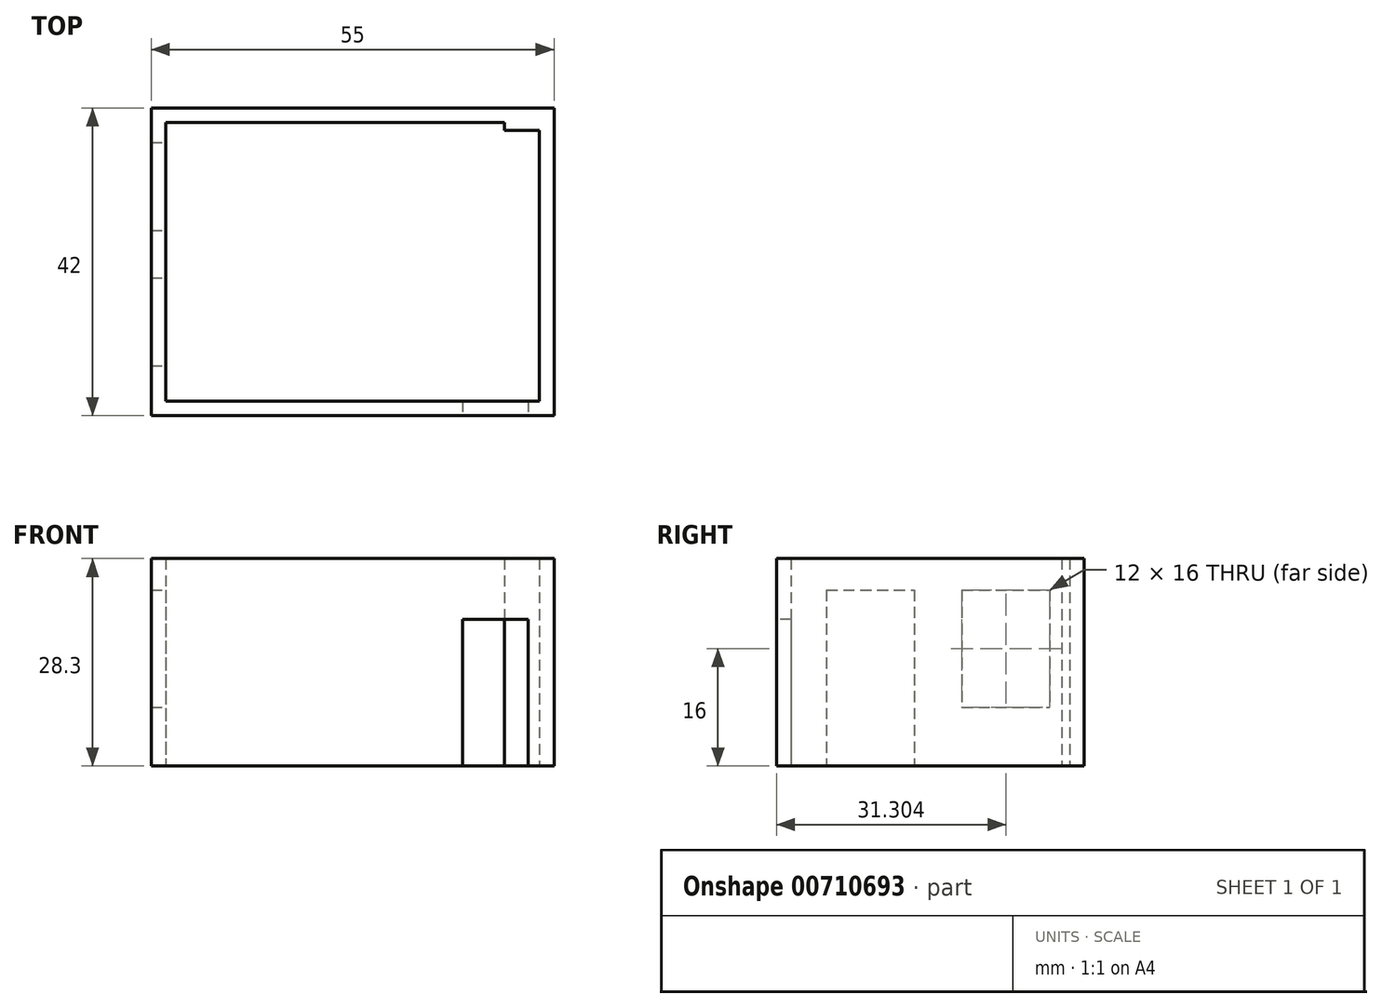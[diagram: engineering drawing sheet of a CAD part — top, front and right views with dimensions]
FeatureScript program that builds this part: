
annotation { "Feature Type Name" : "Feature", "Feature Type Description" : "" }
export const myFeature = defineFeature(function(context is Context, id is Id, definition is map)
    precondition{}
    {
        {
            var Q0;
            Q0=qCreatedBy(makeId("Top.planeOp"),FACE);
            var sketch = newSketch(context, id + "F0", { "sketchPlane" : qUnion([Q0])});
            skLineSegment(sketch, "E0.bottom", {"start": v(0.05, 41.89) * mm, "end": v(55.05, 41.89) * mm});
            skLineSegment(sketch, "E0.top", {"start": v(0.05, -0.11) * mm, "end": v(42.53, -0.11) * mm});
            skLineSegment(sketch, "E0.left", {"start": v(0.05, 41.89) * mm, "end": v(0.05, 37.2) * mm});
            skLineSegment(sketch, "E0.right", {"start": v(55.05, 41.89) * mm, "end": v(55.05, -0.11) * mm});
            skLineSegment(sketch, "E1.0", {"start": v(2.05, 39.89) * mm, "end": v(48.26, 39.89) * mm});
            skLineSegment(sketch, "E1.1", {"start": v(2.05, 39.89) * mm, "end": v(2.05, 37.2) * mm});
            skLineSegment(sketch, "E1.2", {"start": v(2.05, 1.89) * mm, "end": v(42.53, 1.89) * mm});
            skLineSegment(sketch, "E1.3", {"start": v(53.05, 38.83) * mm, "end": v(53.05, 1.89) * mm});
            skLineSegment(sketch, "E2", {"start": v(51.53, 1.89) * mm, "end": v(51.53, -0.11) * mm});
            skLineSegment(sketch, "E3", {"start": v(42.53, 1.89) * mm, "end": v(42.53, -0.11) * mm});
            skLineSegment(sketch, "E4", {"start": v(0.05, 37.2) * mm, "end": v(2.05, 37.2) * mm});
            skLineSegment(sketch, "E5", {"start": v(0.05, 25.2) * mm, "end": v(2.05, 25.2) * mm});
            skLineSegment(sketch, "E6", {"start": v(0.05, 18.72) * mm, "end": v(2.05, 18.72) * mm});
            skLineSegment(sketch, "E7", {"start": v(0.05, 6.72) * mm, "end": v(2.05, 6.72) * mm});
            skLineSegment(sketch, "E8.top", {"start": v(48.26, 38.83) * mm, "end": v(53.05, 38.83) * mm});
            skLineSegment(sketch, "E8.left", {"start": v(48.26, 39.89) * mm, "end": v(48.26, 38.83) * mm});
            skLineSegment(sketch, "E9.trimOffspring", {"start": v(51.53, -0.11) * mm, "end": v(55.05, -0.11) * mm});
            skLineSegment(sketch, "E10.trimOffspring", {"start": v(51.53, 1.89) * mm, "end": v(53.05, 1.89) * mm});
            skLineSegment(sketch, "E11.trimOffspring", {"start": v(2.05, 25.2) * mm, "end": v(2.05, 18.72) * mm});
            skLineSegment(sketch, "E12.trimOffspring", {"start": v(0.05, 25.2) * mm, "end": v(0.05, 18.72) * mm});
            skLineSegment(sketch, "E13.trimOffspring", {"start": v(0.05, 6.72) * mm, "end": v(0.05, -0.11) * mm});
            skLineSegment(sketch, "E14.trimOffspring", {"start": v(2.05, 6.72) * mm, "end": v(2.05, 1.89) * mm});
            skSolve(sketch);
        }
        {
            var Q0;
            Q0 = qSketchRegion(id + "F0", true);
            extrude(context, id + "F1", {"entities" : qUnion([Q0]), "depth" : 28.3 * mm, "offsetDistance" : 25 * mm});
        }
        {
            var Q0;
            Q0=makeQuery(id+"F1.opExtrude","SWEPT_FACE",FACE,{"disambiguationData":[OSD([sQuery(id+"F0.wireOp",EDGE,"E4")])]});
            var sketch = newSketch(context, id + "F2", { "sketchPlane" : qUnion([Q0])});
            skLineSegment(sketch, "E15.bottom", {"start": v(0.05, 8) * mm, "end": v(2.05, 8) * mm});
            skLineSegment(sketch, "E15.top", {"start": v(0.05, 0) * mm, "end": v(2.05, 0) * mm});
            skLineSegment(sketch, "E15.left", {"start": v(0.05, 8) * mm, "end": v(0.05, 0) * mm});
            skLineSegment(sketch, "E15.right", {"start": v(2.05, 8) * mm, "end": v(2.05, 0) * mm});
            skLineSegment(sketch, "E16.0", {"start": v(2.05, 28.3) * mm, "end": v(2.05, 0) * mm});
            skLineSegment(sketch, "E17.0", {"start": v(0.05, 28.3) * mm, "end": v(0.05, 0) * mm});
            skSolve(sketch);
        }
        {
            var Q0;
            Q0=makeQuery(id+"F2.imprint","IMPRINT",FACE,{"disambiguationData":[TD([[makeQuery(id+"F2.imprint","IMPRINT",EDGE,{"derivedFrom":sQuery(id+"F2.wireOp",EDGE,"E15.bottom")}),-1.0]])]});
            extrude(context, id + "F3", {"entities" : qUnion([Q0]), "operationType" : NewBodyOperationType.ADD, "depth" : 12 * mm, "offsetDistance" : 25 * mm});
        }
        {
            var Q0;
            Q0=makeQuery(id+"F1.opExtrude","SWEPT_FACE",FACE,{"disambiguationData":[OSD([sQuery(id+"F0.wireOp",EDGE,"E4")])]});
            var sketch = newSketch(context, id + "F4", { "sketchPlane" : qUnion([Q0])});
            skLineSegment(sketch, "E18.bottom", {"start": v(0.05, 28.3) * mm, "end": v(2.05, 28.3) * mm});
            skLineSegment(sketch, "E18.top", {"start": v(0.05, 24) * mm, "end": v(2.05, 24) * mm});
            skLineSegment(sketch, "E18.left", {"start": v(0.05, 28.3) * mm, "end": v(0.05, 24) * mm});
            skLineSegment(sketch, "E18.right", {"start": v(2.05, 28.3) * mm, "end": v(2.05, 24) * mm});
            skSolve(sketch);
        }
        {
            var Q0;
            Q0=makeQuery(id+"F4.imprint","IMPRINT",FACE,{"disambiguationData":[TD([[makeQuery(id+"F4.imprint","IMPRINT",EDGE,{"derivedFrom":sQuery(id+"F4.wireOp",EDGE,"E18.bottom")}),-1.0]])]});
            extrude(context, id + "F5", {"entities" : qUnion([Q0]), "operationType" : NewBodyOperationType.ADD, "depth" : 35 * mm, "offsetDistance" : 25 * mm});
        }
        {
            var Q0;
            Q0=makeQuery(id+"F1.opExtrude","SWEPT_FACE",FACE,{"disambiguationData":[OSD([sQuery(id+"F0.wireOp",EDGE,"E2")])]});
            var sketch = newSketch(context, id + "F6", { "sketchPlane" : qUnion([Q0])});
            skLineSegment(sketch, "E19.bottom", {"start": v(-1.89, 28.3) * mm, "end": v(0.11, 28.3) * mm});
            skLineSegment(sketch, "E19.top", {"start": v(-1.89, 20) * mm, "end": v(0.11, 20) * mm});
            skLineSegment(sketch, "E19.left", {"start": v(-1.89, 28.3) * mm, "end": v(-1.89, 20) * mm});
            skLineSegment(sketch, "E19.right", {"start": v(0.11, 28.3) * mm, "end": v(0.11, 20) * mm});
            skSolve(sketch);
        }
        {
            var Q0;
            Q0=makeQuery(id+"F6.imprint","IMPRINT",FACE,{"disambiguationData":[TD([[makeQuery(id+"F6.imprint","IMPRINT",EDGE,{"derivedFrom":sQuery(id+"F6.wireOp",EDGE,"E19.bottom")}),-1.0]])]});
            extrude(context, id + "F7", {"entities" : qUnion([Q0]), "operationType" : NewBodyOperationType.ADD, "depth" : 25 * mm, "offsetDistance" : 25 * mm});
        }
    });
